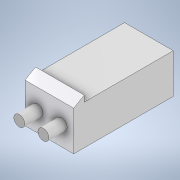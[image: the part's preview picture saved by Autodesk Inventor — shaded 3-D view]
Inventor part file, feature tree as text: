
AUTODESK INVENTOR PART (.ipt)
format: ipt  version: 2020 (Build 240168000, 168)  size: 153,088 bytes
history: native  units: mm
features: extrude x4, sketch x4, projected_geometry x3, other x1
ambient origin geometry x8: Origin, YZ Plane, XZ Plane, XY Plane, X Axis, Y Axis, Z Axis, Center Point
bodies: Body1 (feature_tree)
feature tree (12):
  other  "Sólido1"
  extrude  "Extrusión1"  Depth=16.35mm
  extrude  "Extrusión2"  Depth=8.0mm
  extrude  "Extrusión3"  Depth=6.5mm
  extrude  "Extrusión4"  Depth=3.0mm TaperAngle=0.0deg
  sketch  "Boceto1"  dims[d0=16.35mm d1=16.0mm]
  sketch  "Boceto2"  dims[d2=8.0mm d3=8.175mm]
  projected_geometry  "Contorno proyectado1"
  sketch  "Boceto3"  dims[d4=6.5mm d5=0.0mm d6=7.5mm]
  projected_geometry  "Contorno proyectado2"
  sketch  "Boceto4"  dims[d7=60.0deg d8=16.0mm d9=0.0mm d10=3.25mm d12=3.96mm d13=3.96mm d14=2.06mm d15=1.8mm d16=1.8mm d17=1.8mm d18=1.8mm d19=3.0mm d20=0.0mm d21=40.0mm d22=0.0mm]
  projected_geometry  "Contorno proyectado3"
